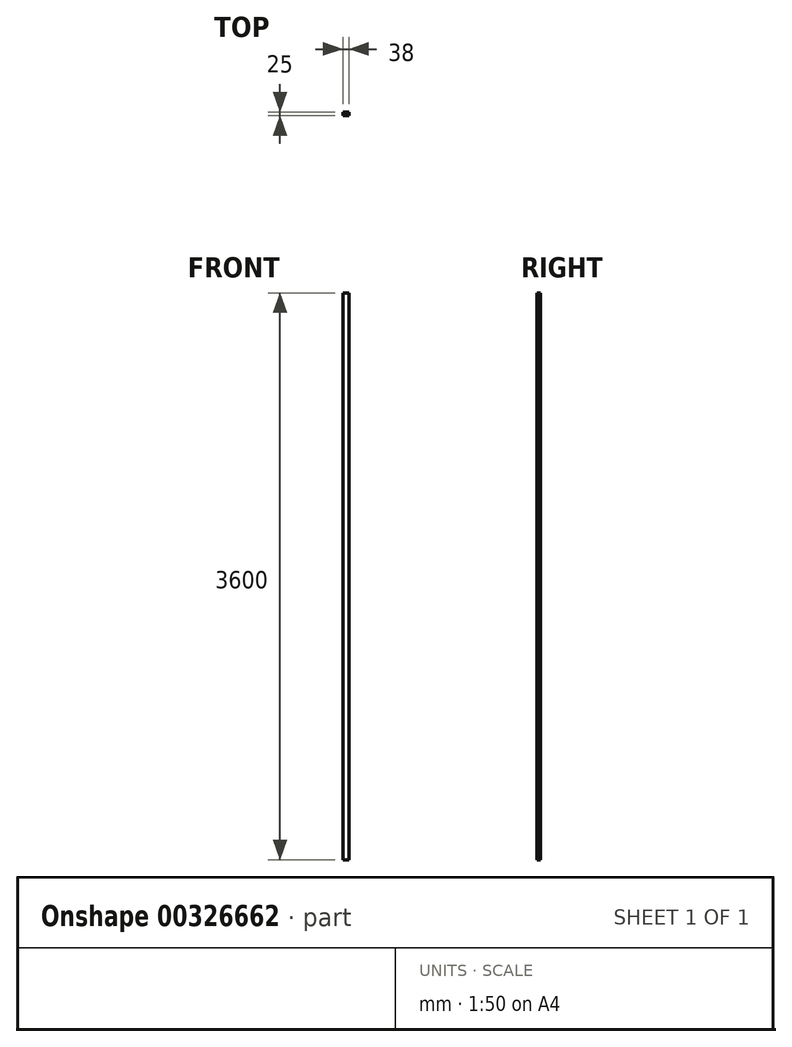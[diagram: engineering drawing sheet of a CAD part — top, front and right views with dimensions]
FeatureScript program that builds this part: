
annotation { "Feature Type Name" : "Feature", "Feature Type Description" : "" }
export const myFeature = defineFeature(function(context is Context, id is Id, definition is map)
    precondition{}
    {
        {
            var Q0;
            Q0=qCreatedBy(makeId("Top.planeOp"),FACE);
            var sketch = newSketch(context, id + "F0", { "sketchPlane" : qUnion([Q0])});
            skLineSegment(sketch, "E0.bottom", {"start": v(0, 0) * mm, "end": v(38, 0) * mm});
            skLineSegment(sketch, "E0.top", {"start": v(0, 25) * mm, "end": v(38, 25) * mm});
            skLineSegment(sketch, "E0.left", {"start": v(0, 0) * mm, "end": v(0, 25) * mm});
            skLineSegment(sketch, "E0.right", {"start": v(38, 0) * mm, "end": v(38, 25) * mm});
            skSolve(sketch);
        }
        {
            var Q0;
            Q0 = qSketchRegion(id + "F0", true);
            extrude(context, id + "F1", {"entities" : qUnion([Q0]), "depth" : 3600 * mm});
        }
    });
